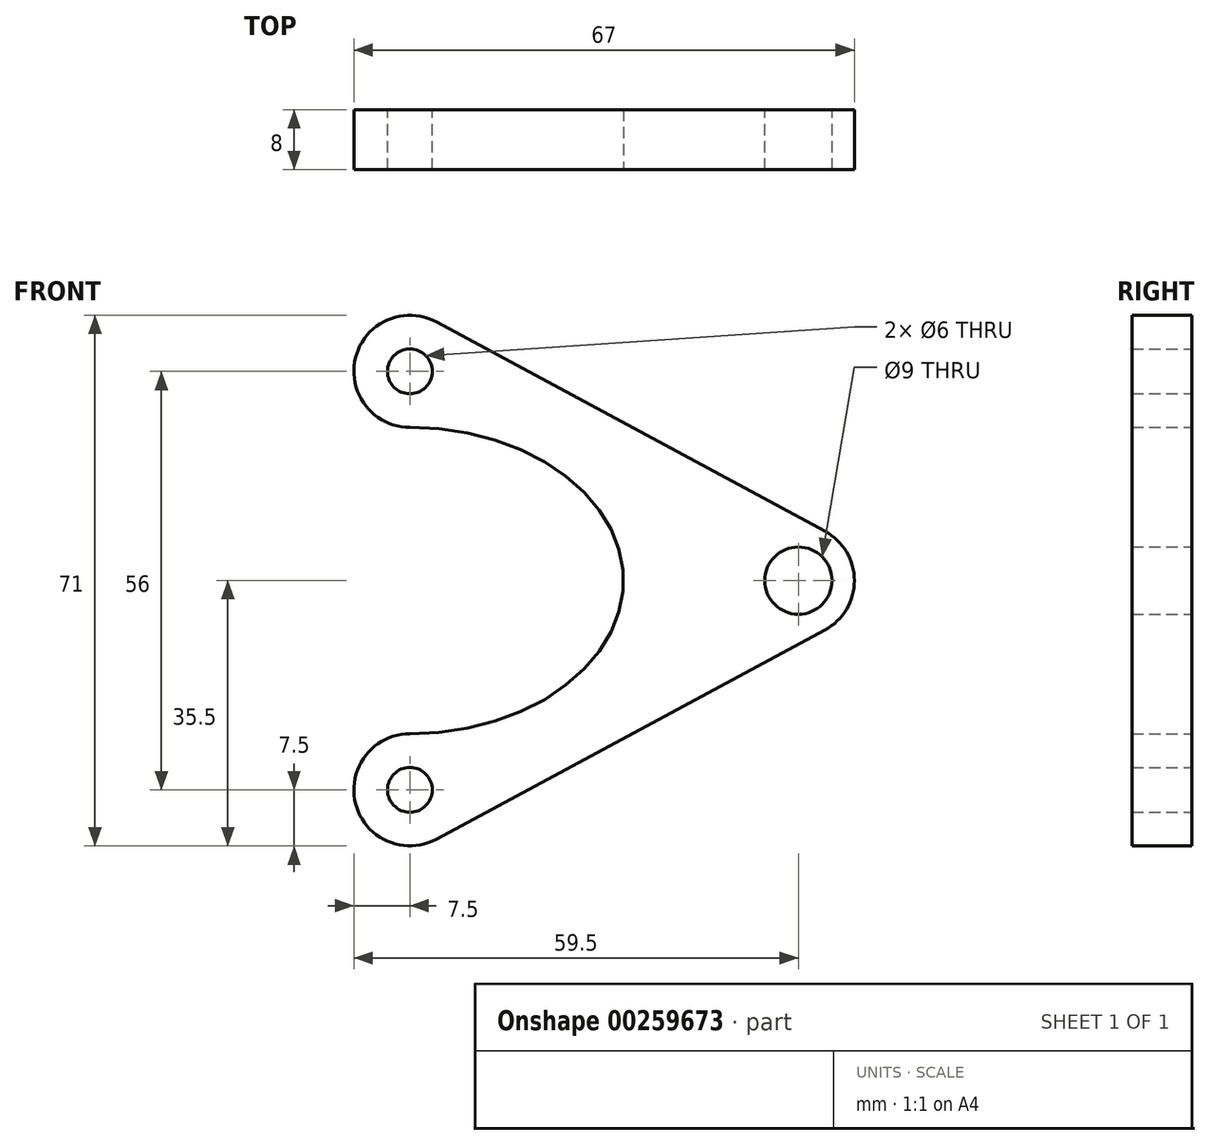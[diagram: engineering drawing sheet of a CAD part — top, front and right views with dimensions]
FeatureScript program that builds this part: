
annotation { "Feature Type Name" : "Feature", "Feature Type Description" : "" }
export const myFeature = defineFeature(function(context is Context, id is Id, definition is map)
    precondition{}
    {
        {
            var Q0;
            Q0=qCreatedBy(makeId("Front.planeOp"),FACE);
            var sketch = newSketch(context, id + "F0", { "sketchPlane" : qUnion([Q0])});
            skCircle(sketch, "E0", {"center": v(0, 28) * mm, "radius": 3 * mm});
            skCircle(sketch, "E1", {"center": v(0, -28) * mm, "radius": 3 * mm});
            skCircle(sketch, "E2", {"center": v(52, 0) * mm, "radius": 4.5 * mm});
            skCircle(sketch, "E3", {"center": v(0, 28) * mm, "radius": 7.5 * mm});
            skCircle(sketch, "E4", {"center": v(52, 0) * mm, "radius": 7.5 * mm});
            skCircle(sketch, "E5", {"center": v(0, -28) * mm, "radius": 7.5 * mm});
            skLineSegment(sketch, "E6", {"start": v(55.56, -6.6) * mm, "end": v(3.56, -34.6) * mm});
            skLineSegment(sketch, "E7", {"start": v(3.56, -34.6) * mm, "end": v(3.56, -34.6) * mm});
            skLineSegment(sketch, "E8", {"start": v(3.56, 34.6) * mm, "end": v(55.56, 6.6) * mm});
            skEllipticalArc(sketch, "E9", {});
            const initialGuessF0  = {"E9": [0, 0, 1, 0, 0.028562523483407935, 0.0205, 4.71238898038469, 1.5707963267948966]};
            skSetInitialGuess(sketch, initialGuessF0);
            skSolve(sketch);
        }
        {
            var Q0;
            Q0=qSketchRegion(id+"F0",true);
            extrude(context, id + "F1", {"entities" : qUnion([Q0]), "depth" : 8 * mm});
        }
    });
